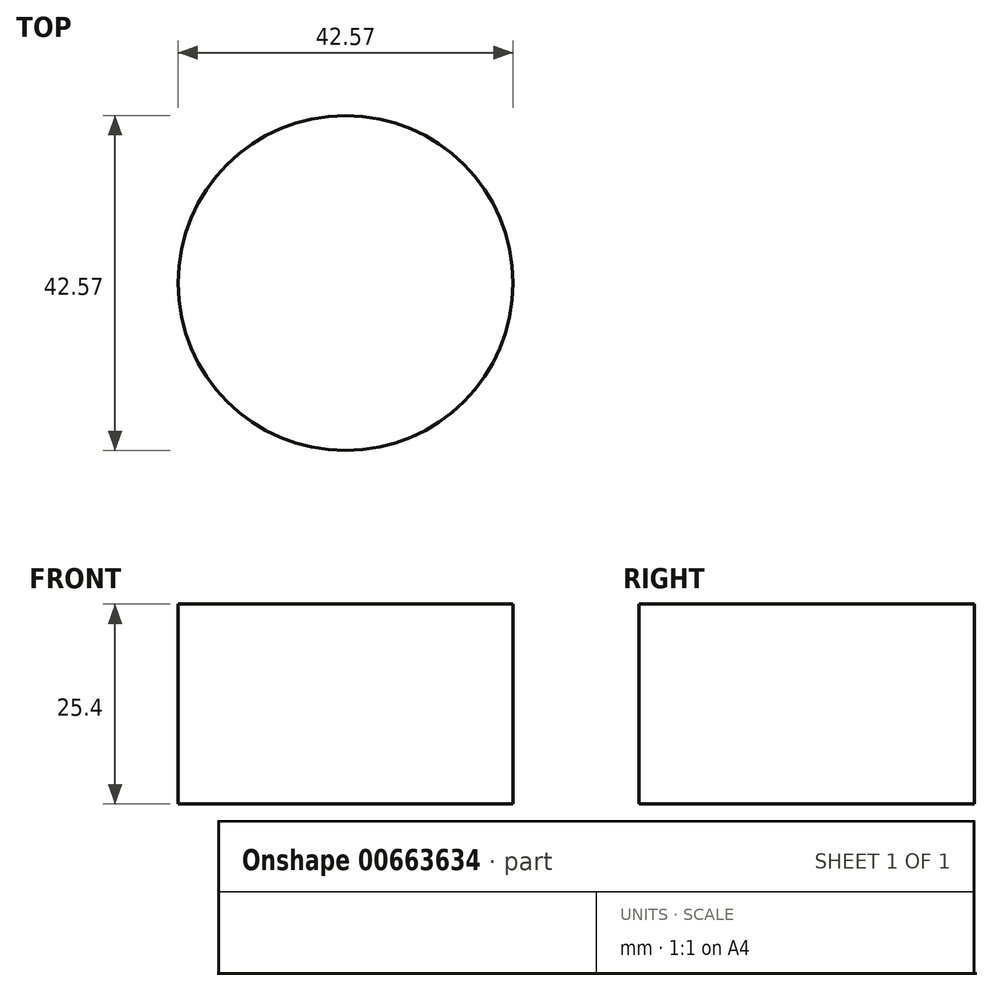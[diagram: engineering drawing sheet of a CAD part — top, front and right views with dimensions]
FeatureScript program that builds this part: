
annotation { "Feature Type Name" : "Feature", "Feature Type Description" : "" }
export const myFeature = defineFeature(function(context is Context, id is Id, definition is map)
    precondition{}
    {
        {
            var Q0;
            Q0=qCreatedBy(makeId("Top.planeOp"),FACE);
            var sketch = newSketch(context, id + "F0", { "sketchPlane" : qUnion([Q0])});
            skCircle(sketch, "E0", {"center": v(-42.57, 19.9) * mm, "radius": 21.28 * mm});
            skSolve(sketch);
        }
        {
            var Q0;
            Q0=makeQuery(id+"F0.imprint","IMPRINT",FACE,{"disambiguationData":[TD([[makeQuery(id+"F0.imprint","IMPRINT",EDGE,{"derivedFrom":sQuery(id+"F0.wireOp",EDGE,"E0")}),1.0]])]});
            extrude(context, id + "F1", {"entities" : qUnion([Q0]), "depth" : 25.4 * mm, "offsetDistance" : 25.4 * mm});
        }
    });
